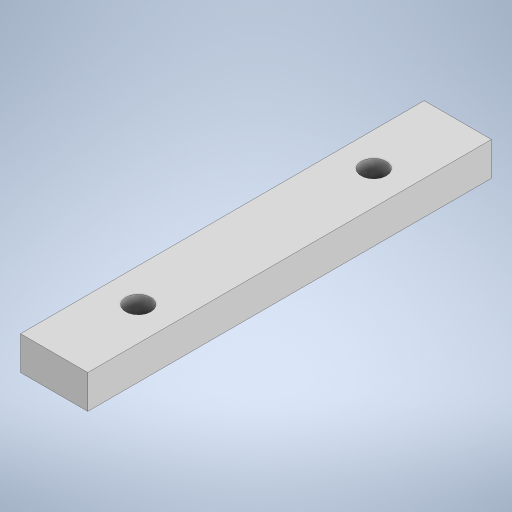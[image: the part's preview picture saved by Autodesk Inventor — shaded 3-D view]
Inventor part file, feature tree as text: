
AUTODESK INVENTOR PART (.ipt)
format: ipt  version: 2024 (Build 280153000, 153)  size: 227,328 bytes
history: native  units: mm
features: extrude x2
ambient origin geometry x8: Origin, YZ Plane, XZ Plane, XY Plane, X Axis, Y Axis, Z Axis, Center Point
bodies: Solid1 (feature_tree)
feature tree (2):
  extrude  "Extrusion1"  Depth=25.4mm
  extrude  "Extrusion2"  Depth=50.8mm
